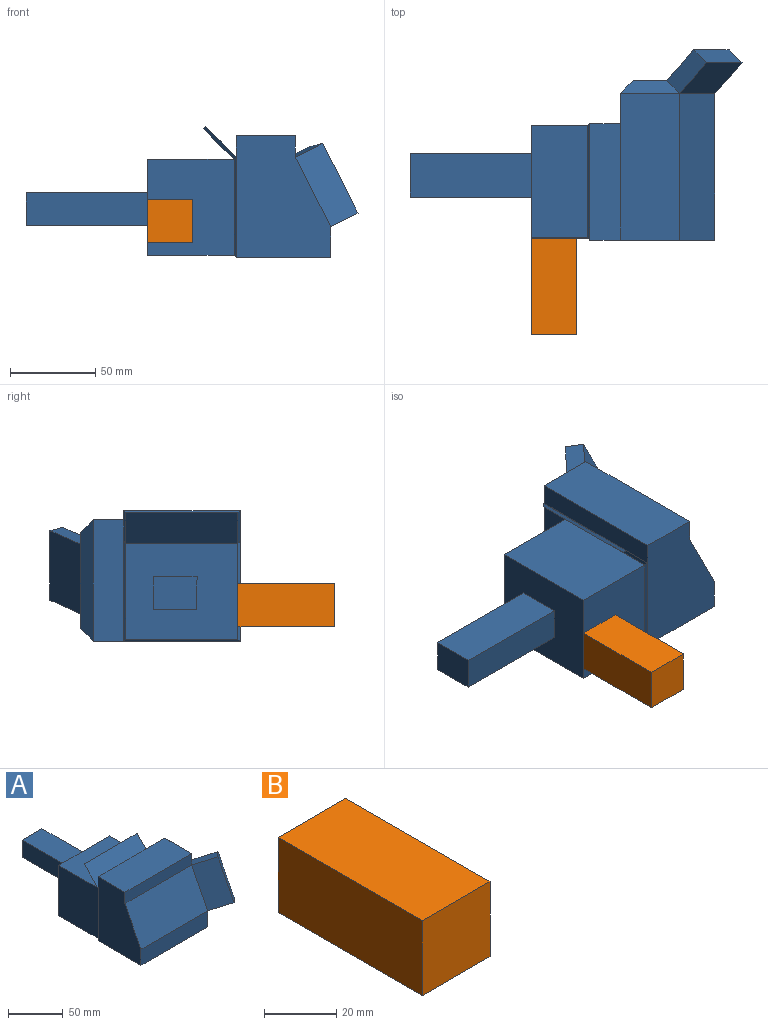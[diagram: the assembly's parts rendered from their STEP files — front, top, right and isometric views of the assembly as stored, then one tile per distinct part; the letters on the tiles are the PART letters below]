
ASSEMBLY  parts=2 mates=1
PART A: 36 faces, bbox 111.7x194.9x76.7 mm
  f0: plane 86.1x17.88mm, normal (0,-1,0), area 1539.2mm2, adj f1,f2,f3,f21
  f1: plane 71.42x55.39mm, normal (-1,0,0), area 3271.3mm2, adj f0,f2,f3,f5,f7,f9,f10
  f2: plane 86.1x55.39mm, normal (0,0,-1), area 4769.5mm2, adj f0,f1,f4,f7,f23
  f3: plane 86.1x40.84mm, normal (0,-0.89,0.45), area 3941.5mm2, adj f0,f1,f9,f27
  f4: plane 68.32x1.27mm, normal (0,0.71,-0.71), area 120.4mm2, adj f2,f5,f6,f13
  f5: plane 58.72x1.27mm, normal (-0.71,0.71,0), area 103.2mm2, adj f1,f4,f14,f17
  f6: plane 58.72x1.27mm, normal (0.71,0.71,0), area 103.2mm2, adj f4,f7,f12,f19
  f7: plane 86.1x71.42mm, normal (0,1,0), area 2137.5mm2, adj f1,f2,f6,f10,f18,f25
  f8: plane 56.18x40.15mm, normal (1,0,0), area 1690.9mm2, adj f21,f22,f23,f24,f25,f29
  f9: plane 86.1x12.7mm, normal (0,-1,0), area 1093.5mm2, adj f1,f3,f10,f22
  f10: plane 86.1x34.72mm, normal (0,0,1), area 2989.1mm2, adj f1,f7,f9,f24
  f11: plane 65.78x50.8mm, normal (0,0,1), area 3341.6mm2, adj f12,f14,f15,f16
  f12: plane 56.18x50.8mm, normal (1,0,0), area 2853.9mm2, adj f6,f11,f13,f15
  f13: plane 65.78x50.8mm, normal (0,0,-1), area 3341.6mm2, adj f4,f12,f14,f15
  f14: plane 56.18x50.8mm, normal (-1,0,0), area 2853.9mm2, adj f5,f11,f13,f15
  f15: plane 65.78x56.18mm, normal (0,1,0), area 3201.9mm2, adj f11,f12,f13,f14,f31,f32,f33,f34
  f16: plane 65.78x17.96mm, normal (0,0.71,-0.71), area 1670.8mm2, adj f11,f17,f19,f20
  f17: plane 19.23x19.23mm, normal (-0.82,0.41,-0.41), area 55.9mm2, adj f5,f16,f18,f20
  f18: plane 68.32x17.96mm, normal (0,-0.71,0.71), area 1735.3mm2, adj f7,f17,f19,f20
  f19: plane 19.23x19.23mm, normal (0.82,0.41,-0.41), area 55.9mm2, adj f6,f16,f18,f20
  f20: plane 68.32x1.27mm, normal (0,0.71,0.71), area 120.4mm2, adj f16,f17,f18,f19
  f21: plane 17.88x7.62mm, normal (0.71,-0.71,0), area 141.8mm2, adj f0,f8,f23,f28
  f22: plane 14.52x7.62mm, normal (0.71,-0.71,0), area 105.6mm2, adj f8,f9,f24,f26
  f23: plane 55.39x7.62mm, normal (0.71,0,-0.71), area 514.8mm2, adj f2,f8,f21,f25
  f24: plane 34.72x7.62mm, normal (0.71,0,0.71), area 292mm2, adj f8,f10,f22,f25
  f25: plane 71.42x7.62mm, normal (0.71,0.71,0), area 687.5mm2, adj f7,f8,f23,f24
  f26: plane 25.58x23.64mm, normal (-0.12,0.34,0.93), area 277.6mm2, adj f22,f27,f29,f30
  f27: plane 48.95x36.7mm, normal (-0.71,-0.63,0.32), area 1162.8mm2, adj f3,f26,f28,f30
  f28: plane 25.58x23.64mm, normal (0.12,-0.34,-0.93), area 277.6mm2, adj f21,f27,f29,f30
  f29: plane 48.95x36.7mm, normal (0.71,0.63,-0.32), area 1162.8mm2, adj f8,f26,f28,f30
  f30: plane 42.66x28.3mm, normal (0.71,-0.63,0.32), area 493.3mm2, adj f26,f27,f28,f29
  f31: plane 71.39x19.32mm, normal (-1,0,-0.02), area 1379.6mm2, adj f15,f32,f34,f35
  f32: plane 71.39x25.76mm, normal (0,0,1), area 1839mm2, adj f15,f31,f33,f35
  f33: plane 71.39x19.32mm, normal (1,0,0), area 1379.2mm2, adj f15,f32,f34,f35
  f34: plane 71.39x25.33mm, normal (0,0,-1), area 1808.5mm2, adj f15,f31,f33,f35
  f35: plane 25.76x19.32mm, normal (0,1,0), area 493.5mm2, adj f31,f32,f33,f34
PART B: 6 faces, bbox 26.5x56.4x25.4 mm
  f0: plane 56.41x25.4mm, normal (1,0,0), area 1432.8mm2, adj f1,f3,f4,f5
  f1: plane 26.52x25.4mm, normal (0,1,0), area 673.6mm2, adj f0,f2,f4,f5
  f2: plane 56.41x25.4mm, normal (-1,0,0), area 1432.8mm2, adj f1,f3,f4,f5
  f3: plane 26.52x25.4mm, normal (0,-1,0), area 673.6mm2, adj f0,f2,f4,f5
  f4: plane 56.41x26.52mm, normal (0,0,1), area 1495.9mm2, adj f0,f1,f2,f3
  f5: plane 56.41x26.52mm, normal (0,0,-1), area 1495.9mm2, adj f0,f1,f2,f3
PLACE A rot(axis=(0,0,1),90deg) t=(26.35,51.08,-4.72)mm
PLACE B t=(34.35,-20.73,3.73)mm
MATE slider A.f13 <-> B.f5  axis (0,0,1) through (-50.83,19.54,-3.45)mm
